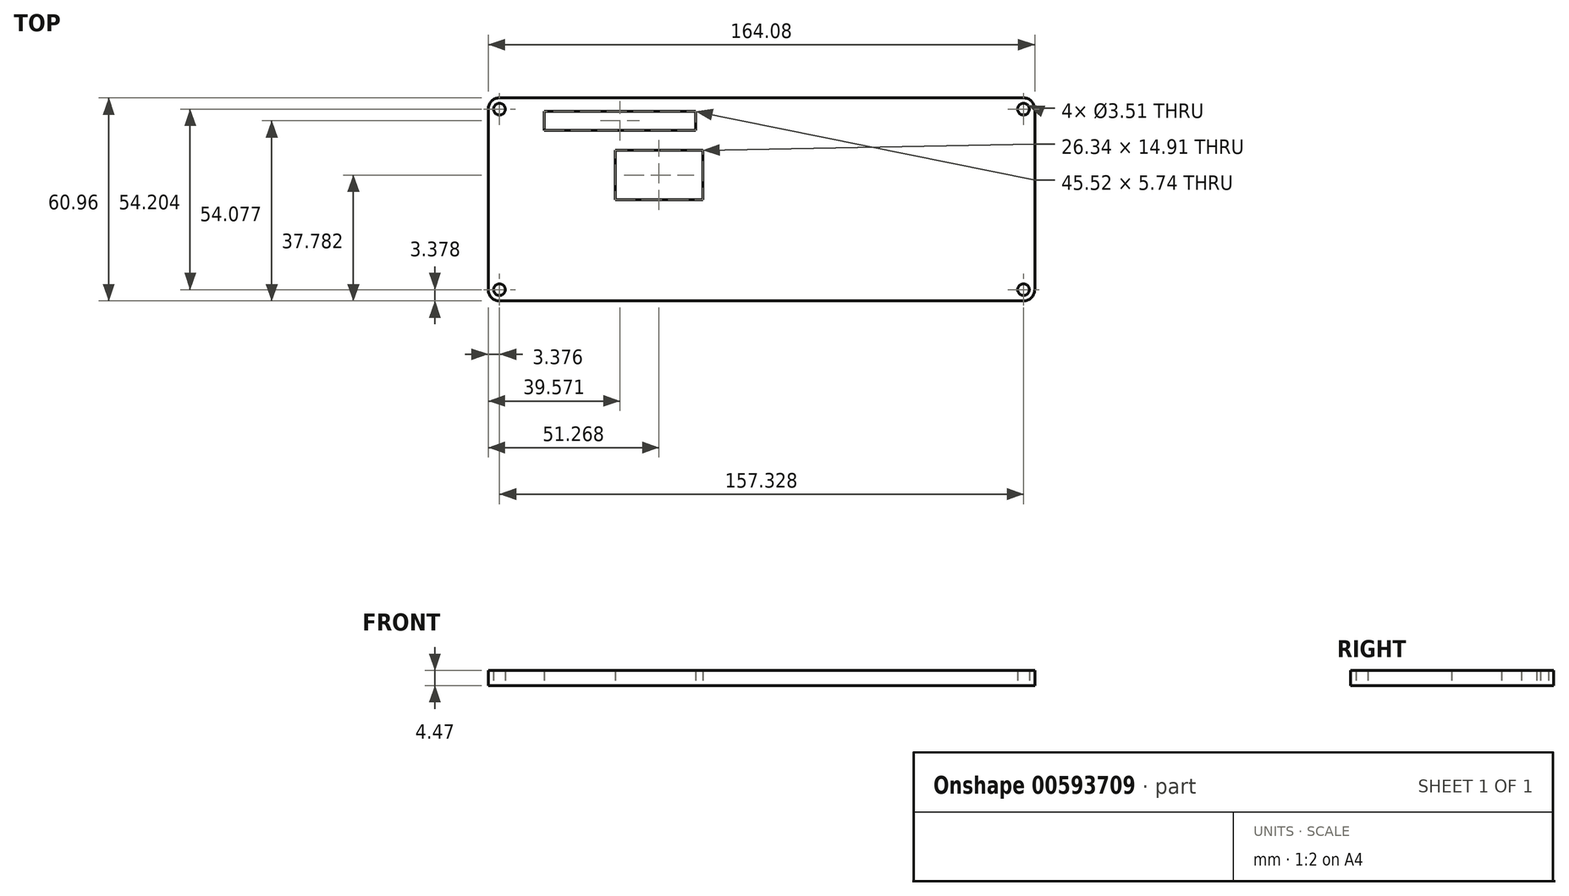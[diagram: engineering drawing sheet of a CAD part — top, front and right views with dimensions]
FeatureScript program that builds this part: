
annotation { "Feature Type Name" : "Feature", "Feature Type Description" : "" }
export const myFeature = defineFeature(function(context is Context, id is Id, definition is map)
    precondition{}
    {
        {
            var Q0;
            Q0=qCreatedBy(makeId("Top.planeOp"),FACE);
            var sketch = newSketch(context, id + "F0", { "sketchPlane" : qUnion([Q0])});
            skLineSegment(sketch, "E0.bottom", {"start": v(78.66, -30.48) * mm, "end": v(-78.66, -30.48) * mm});
            skLineSegment(sketch, "E0.top", {"start": v(78.66, 30.48) * mm, "end": v(-78.66, 30.48) * mm});
            skLineSegment(sketch, "E0.left", {"start": v(82.04, -27.1) * mm, "end": v(82.04, 27.1) * mm});
            skLineSegment(sketch, "E0.right", {"start": v(-82.04, -27.1) * mm, "end": v(-82.04, 27.1) * mm});
            skPoint(sketch, "E0.middle", {"position": v(0, 0) * mm});
            skLineSegment(sketch, "E1.bottom", {"start": v(-65.23, 26.47) * mm, "end": v(-19.71, 26.47) * mm});
            skLineSegment(sketch, "E1.top", {"start": v(-65.23, 20.73) * mm, "end": v(-19.71, 20.73) * mm});
            skLineSegment(sketch, "E1.right", {"start": v(-19.71, 26.47) * mm, "end": v(-19.71, 20.73) * mm});
            skLineSegment(sketch, "E2.bottom", {"start": v(-43.94, 14.76) * mm, "end": v(-17.6, 14.76) * mm});
            skLineSegment(sketch, "E2.top", {"start": v(-43.94, -0.15) * mm, "end": v(-17.6, -0.15) * mm});
            skLineSegment(sketch, "E2.left", {"start": v(-43.94, 14.76) * mm, "end": v(-43.94, -0.15) * mm});
            skLineSegment(sketch, "E2.right", {"start": v(-17.6, 14.76) * mm, "end": v(-17.6, -0.15) * mm});
            skCircle(sketch, "E3", {"center": v(-78.66, 27.1) * mm, "radius": 1.75 * mm});
            skCircle(sketch, "E4", {"center": v(-78.66, -27.1) * mm, "radius": 1.75 * mm});
            skPoint(sketch, "E4.centerSnap0", {"position": v(-78.66, 0) * mm});
            skCircle(sketch, "E5", {"center": v(78.66, 27.1) * mm, "radius": 1.75 * mm});
            skCircle(sketch, "E6", {"center": v(78.66, -27.1) * mm, "radius": 1.75 * mm});
            skLineSegment(sketch, "E7", {"start": v(-65.23, 26.47) * mm, "end": v(-65.23, 20.73) * mm});
            skPoint(sketch, "E8.visualSharp", {"position": v(-82.04, 30.48) * mm});
            skArc(sketch, "E8.filletArc", {"start": v(-78.66, 30.48) * mm, "mid": v(-81.05, 29.5) * mm, "end": v(-82.04, 27.1) * mm});
            skPoint(sketch, "E9.visualSharp", {"position": v(82.04, 30.48) * mm});
            skArc(sketch, "E9.filletArc", {"start": v(82.04, 27.1) * mm, "mid": v(81.05, 29.5) * mm, "end": v(78.66, 30.48) * mm});
            skPoint(sketch, "E10.visualSharp", {"position": v(82.04, -30.48) * mm});
            skArc(sketch, "E10.filletArc", {"start": v(78.66, -30.48) * mm, "mid": v(81.05, -29.5) * mm, "end": v(82.04, -27.1) * mm});
            skPoint(sketch, "E11.visualSharp", {"position": v(-82.04, -30.48) * mm});
            skArc(sketch, "E11.filletArc", {"start": v(-82.04, -27.1) * mm, "mid": v(-81.05, -29.5) * mm, "end": v(-78.66, -30.48) * mm});
            skSolve(sketch);
        }
        {
            var Q0;
            Q0=makeQuery(id+"F0.imprint","IMPRINT",FACE,{"disambiguationData":[TD([[makeQuery(id+"F0.imprint","IMPRINT",EDGE,{"derivedFrom":sQuery(id+"F0.wireOp",EDGE,"E0.bottom")}),-1.0]])]});
            extrude(context, id + "F1", {"entities" : qUnion([Q0]), "depth" : 4.47 * mm, "offsetDistance" : 25.4 * mm});
        }
    });
